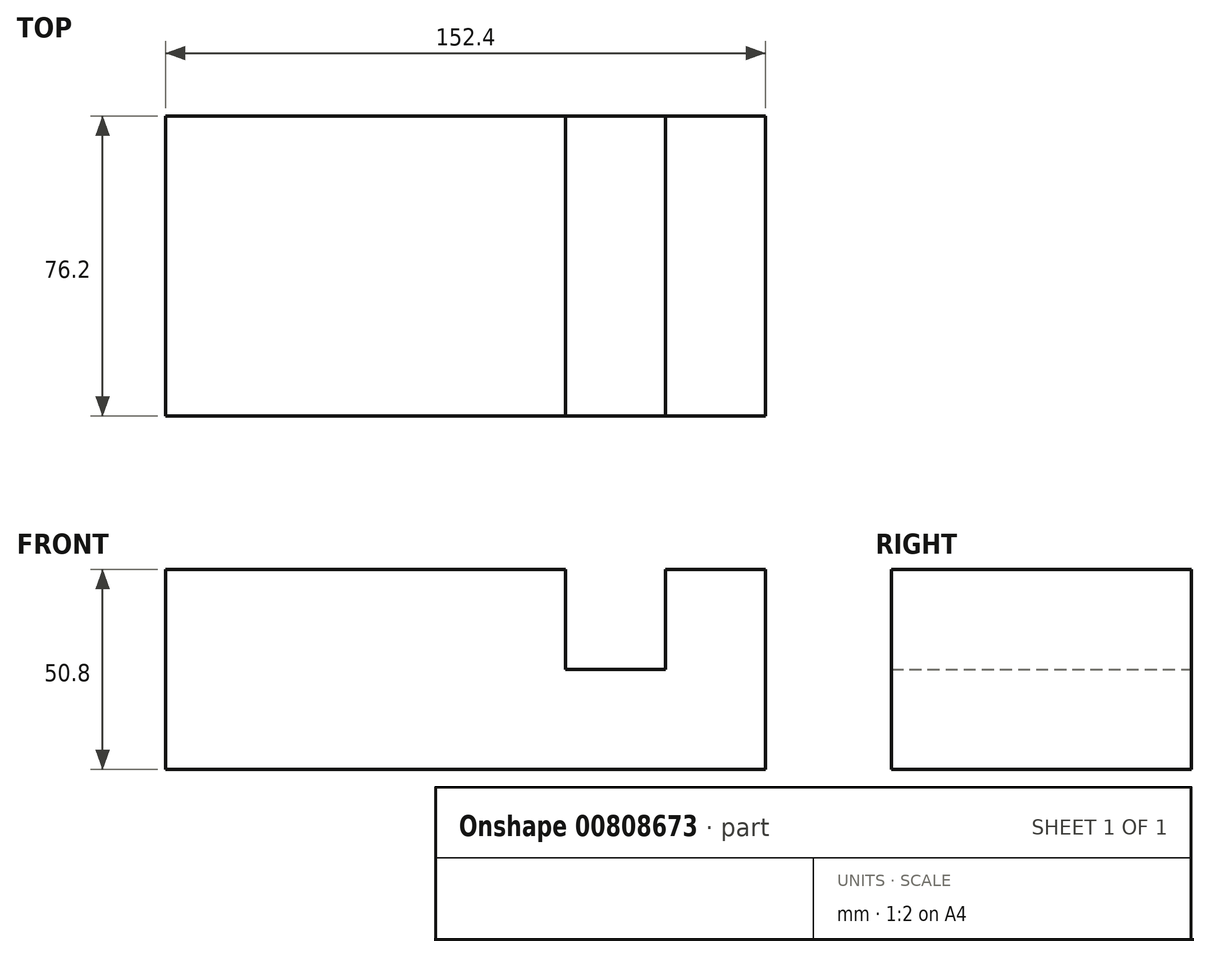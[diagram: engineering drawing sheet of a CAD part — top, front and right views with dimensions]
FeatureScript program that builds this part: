
annotation { "Feature Type Name" : "Feature", "Feature Type Description" : "" }
export const myFeature = defineFeature(function(context is Context, id is Id, definition is map)
    precondition{}
    {
        {
            var Q0;
            Q0=qCreatedBy(makeId("Front.planeOp"),FACE);
            var sketch = newSketch(context, id + "F0", { "sketchPlane" : qUnion([Q0])});
            skLineSegment(sketch, "E0", {"start": v(0, 0) * mm, "end": v(152.4, 0) * mm});
            skLineSegment(sketch, "E1", {"start": v(0, 0) * mm, "end": v(0, 50.8) * mm});
            skLineSegment(sketch, "E2", {"start": v(0, 50.8) * mm, "end": v(101.6, 50.8) * mm});
            skLineSegment(sketch, "E3", {"start": v(101.6, 50.8) * mm, "end": v(101.6, 25.4) * mm});
            skLineSegment(sketch, "E4", {"start": v(101.6, 25.4) * mm, "end": v(127, 25.4) * mm});
            skLineSegment(sketch, "E5", {"start": v(127, 25.4) * mm, "end": v(127, 50.8) * mm});
            skLineSegment(sketch, "E6", {"start": v(127, 50.8) * mm, "end": v(152.4, 50.8) * mm});
            skLineSegment(sketch, "E7", {"start": v(152.4, 50.8) * mm, "end": v(152.4, 0) * mm});
            skSolve(sketch);
        }
        {
            var Q0;
            Q0=makeQuery(id+"F0.imprint","IMPRINT",FACE,{"disambiguationData":[TD([[makeQuery(id+"F0.imprint","IMPRINT",EDGE,{"derivedFrom":sQuery(id+"F0.wireOp",EDGE,"E0")}),1.0]])]});
            extrude(context, id + "F1", {"entities" : qUnion([Q0]), "depth" : 76.2 * mm, "offsetDistance" : 25.4 * mm});
        }
    });
